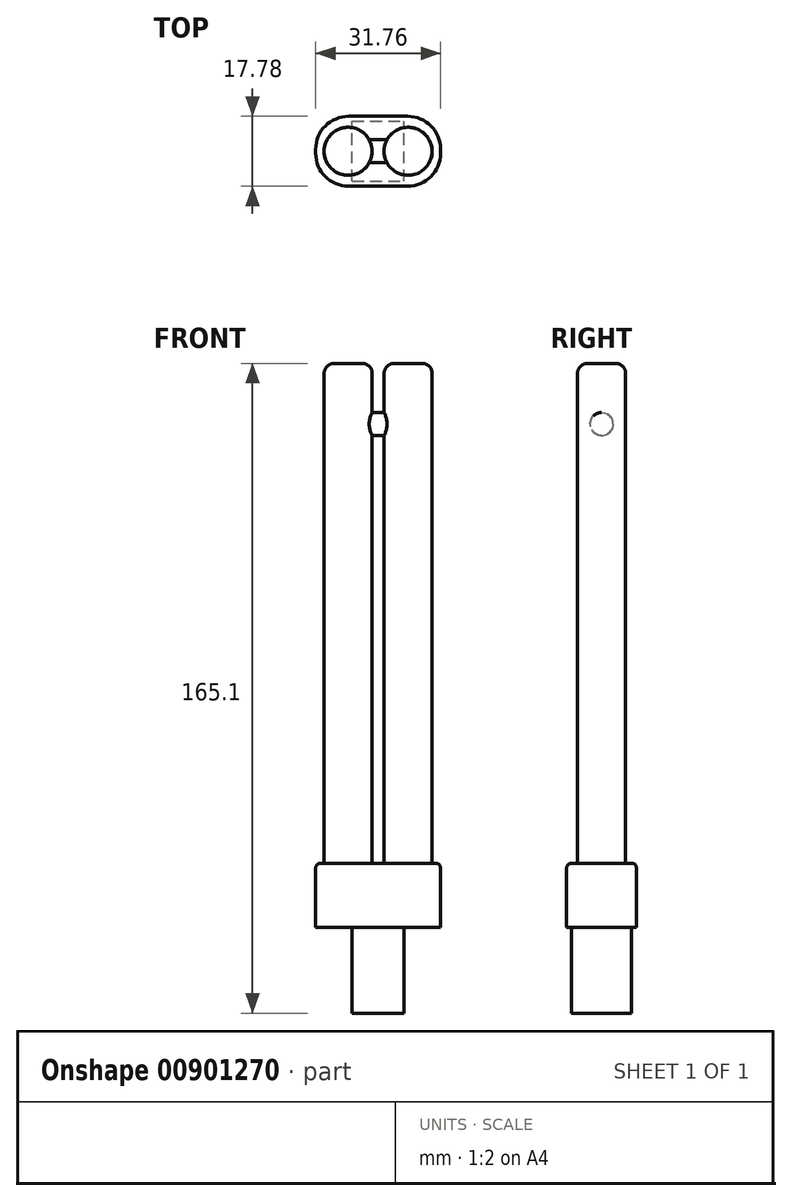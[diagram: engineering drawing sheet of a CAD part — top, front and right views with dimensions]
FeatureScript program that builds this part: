
annotation { "Feature Type Name" : "Feature", "Feature Type Description" : "" }
export const myFeature = defineFeature(function(context is Context, id is Id, definition is map)
    precondition{}
    {
        {
            var Q0;
            Q0=qCreatedBy(makeId("Top.planeOp"),FACE);
            var sketch = newSketch(context, id + "F0", { "sketchPlane" : qUnion([Q0])});
            skCircle(sketch, "E0", {"center": v(7.62, 0) * mm, "radius": 6.1 * mm});
            skCircle(sketch, "E1", {"center": v(-7.62, 0) * mm, "radius": 6.1 * mm});
            skSolve(sketch);
        }
        {
            var Q0;
            Q0 = qSketchRegion(id + "F0", true);
            extrude(context, id + "F1", {"entities" : qUnion([Q0]), "depth" : 127 * mm, "offsetDistance" : 25.4 * mm});
        }
        {
            var Q0;
            Q0=qCreatedBy(makeId("Right.planeOp"),FACE);
            var sketch = newSketch(context, id + "F2", { "sketchPlane" : qUnion([Q0])});
            skCircle(sketch, "E2", {"center": v(0, 111.6) * mm, "radius": 2.92 * mm});
            skSolve(sketch);
        }
        {
            var Q0;
            Q0 = qSketchRegion(id + "F2", true);
            extrude(context, id + "F3", {"entities" : qUnion([Q0]), "operationType" : NewBodyOperationType.ADD, "depth" : 5.08 * mm, "offsetDistance" : 25.4 * mm, "hasSecondDirection" : true, "secondDirectionOppositeDirection" : true, "secondDirectionDepth" : 5.08 * mm});
        }
        {
            var Q0;
            Q0=makeQuery(id+"F1.opExtrude","CAP_FACE",FACE,{"disambiguationData":[OSD([sQuery(id+"F0.wireOp",EDGE,"E1")])],"isStart":false});
            var Q1;
            Q1=makeQuery(id+"F1.opExtrude","CAP_FACE",FACE,{"disambiguationData":[OSD([sQuery(id+"F0.wireOp",EDGE,"E0")])],"isStart":false});
            fillet(context, id + "F4", {"entities" : qUnion([Q0, Q1]), "radius" : 2.54 * mm, "tangentPropagation" : true, "allowEdgeOverflow" : false});
        }
        {
            var Q0;
            Q0=qCreatedBy(makeId("Top.planeOp"),FACE);
            var sketch = newSketch(context, id + "F5", { "sketchPlane" : qUnion([Q0])});
            skLineSegment(sketch, "E3.bottom", {"start": v(-7.5, -8.9) * mm, "end": v(7.5, -8.9) * mm});
            skLineSegment(sketch, "E3.top", {"start": v(-7.5, 8.9) * mm, "end": v(7.5, 8.9) * mm});
            skLineSegment(sketch, "E3.left", {"start": v(-15.88, -0.5) * mm, "end": v(-15.88, 0.5) * mm});
            skLineSegment(sketch, "E3.right", {"start": v(15.88, -0.5) * mm, "end": v(15.88, 0.5) * mm});
            skPoint(sketch, "E3.middle", {"position": v(0, 0) * mm});
            skPoint(sketch, "E4.visualSharp", {"position": v(-15.88, -8.9) * mm});
            skArc(sketch, "E4.filletArc", {"start": v(-15.88, -0.5) * mm, "mid": v(-13.42, -6.43) * mm, "end": v(-7.5, -8.9) * mm});
            skPoint(sketch, "E5.visualSharp", {"position": v(-15.88, 8.9) * mm});
            skArc(sketch, "E5.filletArc", {"start": v(-7.5, 8.9) * mm, "mid": v(-13.42, 6.43) * mm, "end": v(-15.88, 0.5) * mm});
            skPoint(sketch, "E6.visualSharp", {"position": v(15.88, -8.9) * mm});
            skArc(sketch, "E6.filletArc", {"start": v(7.5, -8.9) * mm, "mid": v(13.42, -6.43) * mm, "end": v(15.88, -0.5) * mm});
            skPoint(sketch, "E7.visualSharp", {"position": v(15.88, 8.9) * mm});
            skArc(sketch, "E7.filletArc", {"start": v(15.88, 0.5) * mm, "mid": v(13.42, 6.43) * mm, "end": v(7.5, 8.9) * mm});
            skSolve(sketch);
        }
        {
            var Q0;
            Q0 = qSketchRegion(id + "F5", true);
            extrude(context, id + "F6", {"entities" : qUnion([Q0]), "operationType" : NewBodyOperationType.ADD, "oppositeDirection" : true, "depth" : 16.26 * mm, "offsetDistance" : 25.4 * mm});
        }
        {
            var Q0;
            Q0=makeQuery(id+"F6.opExtrude","CAP_EDGE",EDGE,{"disambiguationData":[OSD([sQuery(id+"F5.wireOp",EDGE,"E3.bottom")])],"isStart":true});
            fillet(context, id + "F7", {"entities" : qUnion([Q0]), "radius" : 1.27 * mm, "tangentPropagation" : true, "allowEdgeOverflow" : false});
        }
        {
            var Q0;
            Q0=makeQuery(id+"F6.opExtrude","CAP_FACE",FACE,{"disambiguationData":[OSD([sQuery(id+"F5.wireOp",EDGE,"E3.bottom"),sQuery(id+"F5.wireOp",EDGE,"E3.top"),sQuery(id+"F5.wireOp",EDGE,"E3.left"),sQuery(id+"F5.wireOp",EDGE,"E3.right"),sQuery(id+"F5.wireOp",EDGE,"E4.filletArc"),sQuery(id+"F5.wireOp",EDGE,"E5.filletArc"),sQuery(id+"F5.wireOp",EDGE,"E6.filletArc"),sQuery(id+"F5.wireOp",EDGE,"E7.filletArc")])],"isStart":false});
            var sketch = newSketch(context, id + "F8", { "sketchPlane" : qUnion([Q0])});
            skLineSegment(sketch, "E8.bottom", {"start": v(-6.6, 7.62) * mm, "end": v(6.6, 7.62) * mm});
            skLineSegment(sketch, "E8.top", {"start": v(-6.6, -7.62) * mm, "end": v(6.6, -7.62) * mm});
            skLineSegment(sketch, "E8.left", {"start": v(-6.6, 7.62) * mm, "end": v(-6.6, -7.62) * mm});
            skLineSegment(sketch, "E8.right", {"start": v(6.6, 7.62) * mm, "end": v(6.6, -7.62) * mm});
            skPoint(sketch, "E8.middle", {"position": v(0, 0) * mm});
            skSolve(sketch);
        }
        {
            var Q0;
            Q0 = qSketchRegion(id + "F8", true);
            extrude(context, id + "F9", {"entities" : qUnion([Q0]), "operationType" : NewBodyOperationType.ADD, "depth" : 21.84 * mm, "offsetDistance" : 25.4 * mm});
        }
    });
